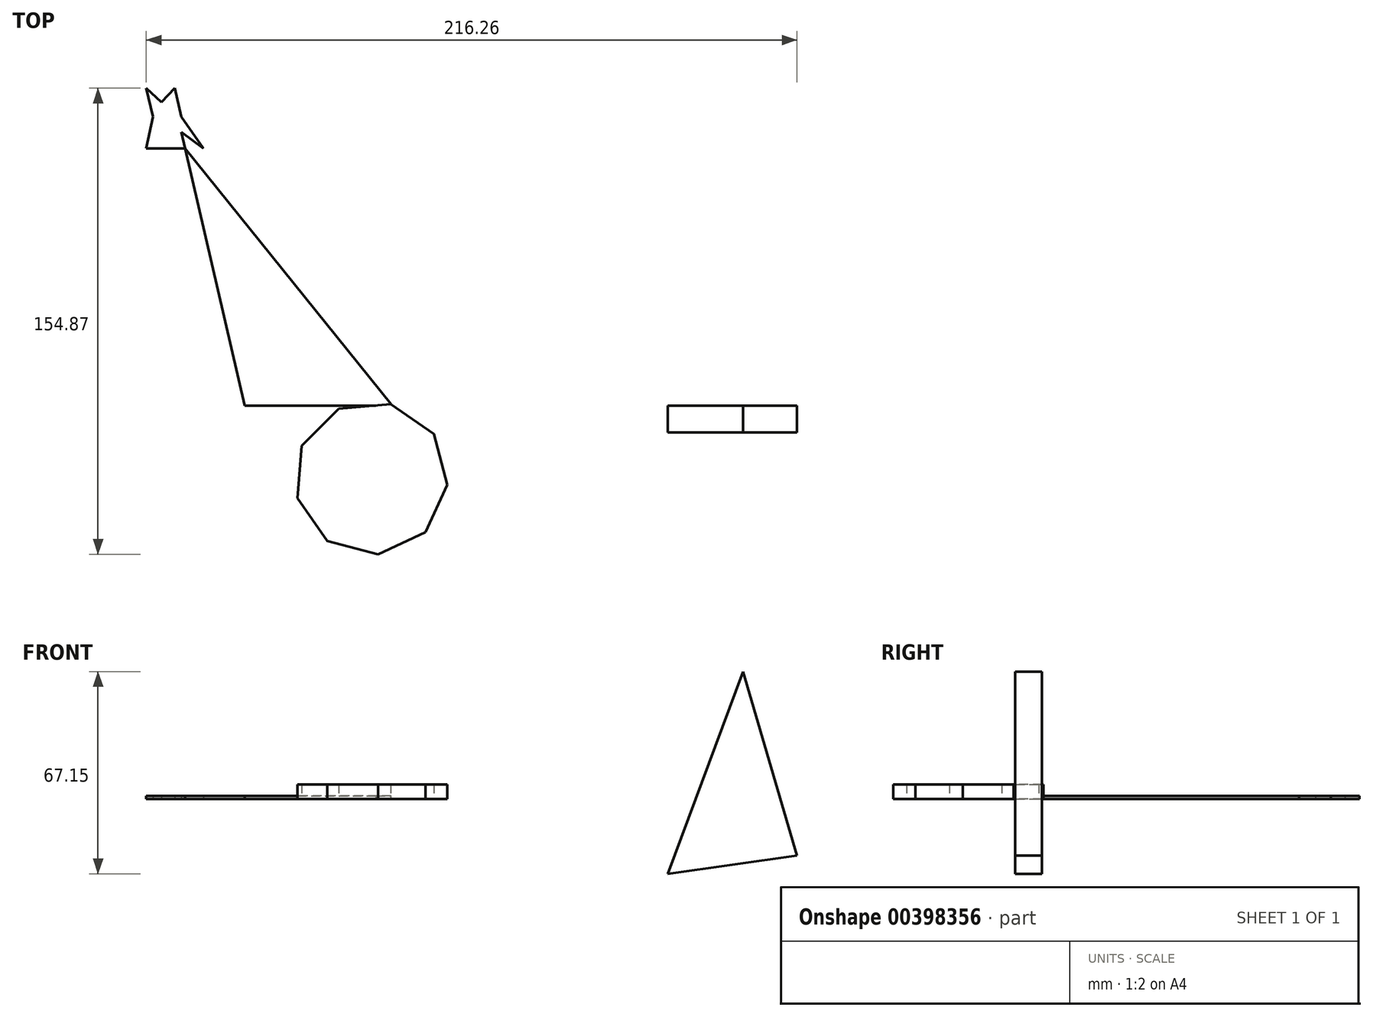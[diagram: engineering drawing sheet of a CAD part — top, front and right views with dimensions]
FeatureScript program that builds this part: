
annotation { "Feature Type Name" : "Feature", "Feature Type Description" : "" }
export const myFeature = defineFeature(function(context is Context, id is Id, definition is map)
    precondition{}
    {
        {
            var Q0;
            Q0=qCreatedBy(makeId("Top.planeOp"),FACE);
            var sketch = newSketch(context, id + "F0", { "sketchPlane" : qUnion([Q0])});
            skCircle(sketch, "E0.cCircle", {"center": v(-70.58, -24.12) * mm, "radius": 23.88 * mm, "construction": true});
            skLineSegment(sketch, "E0.0", {"start": v(-45.26, -26.28) * mm, "end": v(-52.58, -42.05) * mm});
            skLineSegment(sketch, "E0.1", {"start": v(-52.58, -42.05) * mm, "end": v(-68.32, -49.43) * mm});
            skLineSegment(sketch, "E0.2", {"start": v(-68.32, -49.43) * mm, "end": v(-85.12, -44.96) * mm});
            skLineSegment(sketch, "E0.3", {"start": v(-85.12, -44.96) * mm, "end": v(-95.12, -30.74) * mm});
            skLineSegment(sketch, "E0.4", {"start": v(-95.12, -30.74) * mm, "end": v(-93.64, -13.42) * mm});
            skLineSegment(sketch, "E0.5", {"start": v(-93.64, -13.42) * mm, "end": v(-81.37, -1.1) * mm});
            skLineSegment(sketch, "E0.6", {"start": v(-81.37, -1.1) * mm, "end": v(-64.05, 0.45) * mm});
            skLineSegment(sketch, "E0.7", {"start": v(-64.05, 0.45) * mm, "end": v(-49.8, -9.5) * mm});
            skLineSegment(sketch, "E0.8", {"start": v(-49.8, -9.5) * mm, "end": v(-45.26, -26.28) * mm});
            skPoint(sketch, "E0.0.midPoint", {"position": v(-48.92, -34.17) * mm});
            skSolve(sketch);
        }
        {
            var Q0;
            Q0=makeQuery(id+"F0.imprint","IMPRINT",FACE,{"disambiguationData":[TD([[makeQuery(id+"F0.imprint","IMPRINT",EDGE,{"derivedFrom":sQuery(id+"F0.wireOp",EDGE,"E0.0")}),-1.0]])]});
            extrude(context, id + "F1", {"entities" : qUnion([Q0]), "depth" : 2.8 * mm});
        }
        {
            var Q0;
            Q0=qCreatedBy(makeId("Top.planeOp"),FACE);
            var sketch = newSketch(context, id + "F2", { "sketchPlane" : qUnion([Q0])});
            skCircle(sketch, "E1", {"center": v(-76.62, -19.14) * mm, "radius": 5 * mm});
            skSolve(sketch);
        }
        {
            var Q0;
            Q0=makeQuery(id+"F1.opExtrude","CAP_FACE",FACE,{"disambiguationData":[OSD([sQuery(id+"F0.wireOp",EDGE,"E0.0"),sQuery(id+"F0.wireOp",EDGE,"E0.1"),sQuery(id+"F0.wireOp",EDGE,"E0.2"),sQuery(id+"F0.wireOp",EDGE,"E0.3"),sQuery(id+"F0.wireOp",EDGE,"E0.4"),sQuery(id+"F0.wireOp",EDGE,"E0.5"),sQuery(id+"F0.wireOp",EDGE,"E0.6"),sQuery(id+"F0.wireOp",EDGE,"E0.7"),sQuery(id+"F0.wireOp",EDGE,"E0.8")])],"isStart":false});
            extrude(context, id + "F3", {"entities" : qUnion([Q0]), "operationType" : NewBodyOperationType.ADD, "depth" : 2.03 * mm});
        }
        {
            var Q0;
            Q0=sQuery(id+"F2.wireOp",EDGE,"E1");
            extrude(context, id + "F4", {"bodyType" : ToolBodyType.SURFACE, "surfaceEntities" : qUnion([Q0]), "depth" : 13.72 * mm});
        }
        {
            var Q0;
            Q0=qCreatedBy(makeId("Top.planeOp"),FACE);
            var sketch = newSketch(context, id + "F5", { "sketchPlane" : qUnion([Q0])});
            skLineSegment(sketch, "E2", {"start": v(-112.61, 0) * mm, "end": v(-63.67, 0) * mm});
            skLineSegment(sketch, "E3", {"start": v(-63.67, 0) * mm, "end": v(-132.4, 85.41) * mm});
            skLineSegment(sketch, "E4", {"start": v(-132.4, 85.41) * mm, "end": v(-112.61, 0) * mm});
            skLineSegment(sketch, "E5", {"start": v(-132.4, 85.41) * mm, "end": v(-133.68, 90.88) * mm});
            skLineSegment(sketch, "E6", {"start": v(-133.68, 90.88) * mm, "end": v(-126.37, 85.41) * mm});
            skLineSegment(sketch, "E7", {"start": v(-126.37, 85.41) * mm, "end": v(-133.68, 96) * mm});
            skLineSegment(sketch, "E8", {"start": v(-133.68, 96) * mm, "end": v(-135.87, 105.44) * mm});
            skLineSegment(sketch, "E9", {"start": v(-135.87, 105.44) * mm, "end": v(-140.35, 100.72) * mm});
            skPoint(sketch, "E9.endSnap0", {"position": v(-134.77, 100.72) * mm});
            skLineSegment(sketch, "E10", {"start": v(-140.35, 100.72) * mm, "end": v(-145.32, 105.44) * mm});
            skLineSegment(sketch, "E11", {"start": v(-145.32, 105.44) * mm, "end": v(-143.13, 96) * mm});
            skLineSegment(sketch, "E12", {"start": v(-143.13, 96) * mm, "end": v(-145.32, 85.41) * mm});
            skLineSegment(sketch, "E13", {"start": v(-145.32, 85.41) * mm, "end": v(-132.4, 85.41) * mm});
            skSolve(sketch);
        }
        {
            var Q0;
            Q0=makeQuery(id+"F5.imprint","IMPRINT",FACE,{"disambiguationData":[TD([[makeQuery(id+"F5.imprint","IMPRINT",EDGE,{"derivedFrom":sQuery(id+"F5.wireOp",EDGE,"E2")}),1.0]])]});
            var Q1;
            Q1=makeQuery(id+"F5.imprint","IMPRINT",FACE,{"disambiguationData":[TD([[makeQuery(id+"F5.imprint","IMPRINT",EDGE,{"derivedFrom":sQuery(id+"F5.wireOp",EDGE,"E5")}),1.0]])]});
            extrude(context, id + "F6", {"entities" : qUnion([Q0, Q1]), "operationType" : NewBodyOperationType.ADD, "depth" : 1.02 * mm});
        }
        {
            var Q0;
            Q0=qCreatedBy(makeId("Front.planeOp"),FACE);
            var sketch = newSketch(context, id + "F7", { "sketchPlane" : qUnion([Q0])});
            skLineSegment(sketch, "E14", {"start": v(27.94, -24.86) * mm, "end": v(52.97, 42.29) * mm});
            skLineSegment(sketch, "E15", {"start": v(52.97, 42.29) * mm, "end": v(70.94, -18.79) * mm});
            skLineSegment(sketch, "E16", {"start": v(70.94, -18.79) * mm, "end": v(27.94, -24.86) * mm});
            skSolve(sketch);
        }
        {
            var Q0;
            Q0=makeQuery(id+"F7.imprint","IMPRINT",FACE,{"disambiguationData":[TD([[makeQuery(id+"F7.imprint","IMPRINT",EDGE,{"derivedFrom":sQuery(id+"F7.wireOp",EDGE,"E14")}),-1.0]])]});
            extrude(context, id + "F8", {"entities" : qUnion([Q0]), "depth" : 8.9 * mm});
        }
    });
